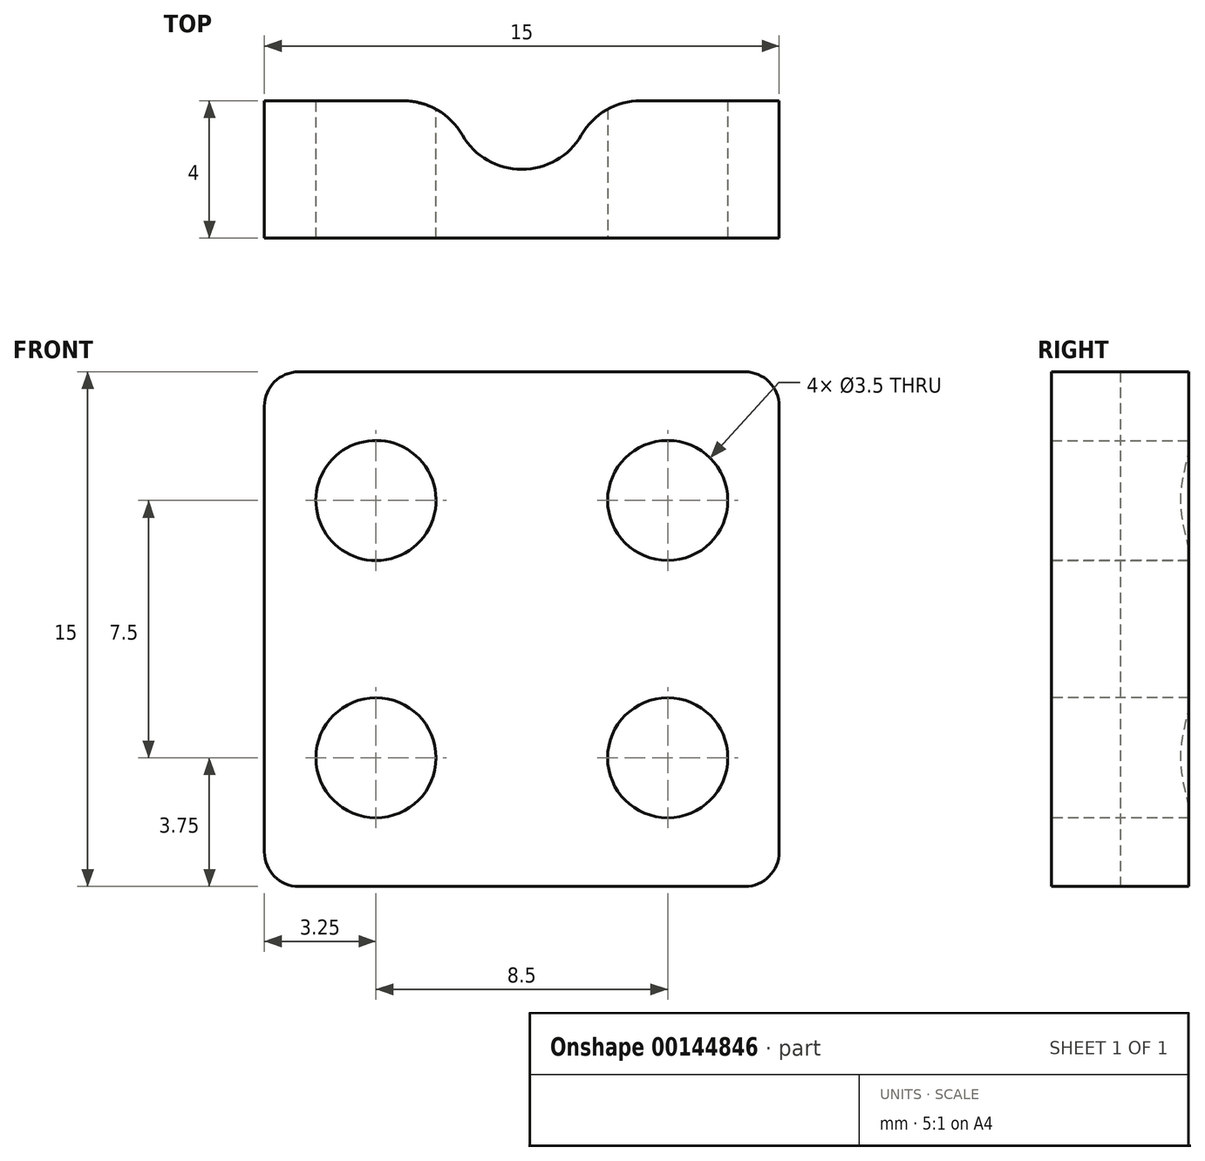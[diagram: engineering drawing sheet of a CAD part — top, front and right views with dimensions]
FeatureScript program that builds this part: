
annotation { "Feature Type Name" : "Feature", "Feature Type Description" : "" }
export const myFeature = defineFeature(function(context is Context, id is Id, definition is map)
    precondition{}
    {
        {
            var Q0;
            Q0=qCreatedBy(makeId("Top.planeOp"),FACE);
            var sketch = newSketch(context, id + "F0", { "sketchPlane" : qUnion([Q0])});
            skLineSegment(sketch, "E0.bottom", {"start": v(7.5, -4) * mm, "end": v(-7.5, -4) * mm});
            skLineSegment(sketch, "E0.top", {"start": v(7.5, 4) * mm, "end": v(-7.5, 4) * mm});
            skLineSegment(sketch, "E0.left", {"start": v(7.5, -4) * mm, "end": v(7.5, 4) * mm});
            skLineSegment(sketch, "E0.right", {"start": v(-7.5, -4) * mm, "end": v(-7.5, 4) * mm});
            skPoint(sketch, "E0.middle", {"position": v(0, 0) * mm});
            skSolve(sketch);
        }
        {
            var Q0;
            Q0=qCreatedBy(makeId("Top.planeOp"),FACE);
            var sketch = newSketch(context, id + "F1", { "sketchPlane" : qUnion([Q0])});
            skCircle(sketch, "E1", {"center": v(0, 0) * mm, "radius": 2 * mm});
            skSolve(sketch);
        }
        {
            var Q0;
            Q0=makeQuery(id+"F0.imprint","IMPRINT",FACE,{"disambiguationData":[TD([[makeQuery(id+"F0.imprint","IMPRINT",EDGE,{"derivedFrom":sQuery(id+"F0.wireOp",EDGE,"E0.bottom")}),-1.0]])]});
            extrude(context, id + "F2", {"entities" : qUnion([Q0]), "depth" : 15 * mm});
        }
        {
            var Q0;
            Q0=makeQuery(id+"F1.imprint","IMPRINT",FACE,{"disambiguationData":[TD([[makeQuery(id+"F1.imprint","IMPRINT",EDGE,{"derivedFrom":sQuery(id+"F1.wireOp",EDGE,"E1")}),1.0]])]});
            extrude(context, id + "F3", {"entities" : qUnion([Q0]), "operationType" : NewBodyOperationType.REMOVE, "depth" : 20 * mm});
        }
        {
            var Q0;
            Q0=qCreatedBy(makeId("Front.planeOp"),FACE);
            var sketch = newSketch(context, id + "F4", { "sketchPlane" : qUnion([Q0])});
            skCircle(sketch, "E2", {"center": v(-4.25, 11.25) * mm, "radius": 1.75 * mm});
            skSolve(sketch);
        }
        {
            var Q0;
            Q0 = qSketchRegion(id + "F4", true);
            extrude(context, id + "F5", {"entities" : qUnion([Q0]), "operationType" : NewBodyOperationType.REMOVE, "depth" : 15 * mm});
        }
        {
            var Q0;
            Q0 = qSketchRegion(id + "F4", true);
            extrude(context, id + "F6", {"entities" : qUnion([Q0]), "operationType" : NewBodyOperationType.REMOVE, "oppositeDirection" : true, "depth" : 25 * mm});
        }
        {
            var Q0;
            Q0=qCreatedBy(makeId("Top.planeOp"),FACE);
            var sketch = newSketch(context, id + "F7", { "sketchPlane" : qUnion([Q0])});
            skLineSegment(sketch, "E3.bottom", {"start": v(9.53, 0) * mm, "end": v(-9.53, 0) * mm});
            skLineSegment(sketch, "E3.top", {"start": v(9.53, 8.77) * mm, "end": v(-9.53, 8.77) * mm});
            skLineSegment(sketch, "E3.left", {"start": v(9.53, 0) * mm, "end": v(9.53, 8.77) * mm});
            skLineSegment(sketch, "E3.right", {"start": v(-9.53, 0) * mm, "end": v(-9.53, 8.77) * mm});
            skPoint(sketch, "E3.middle", {"position": v(0, 4.38) * mm});
            skSolve(sketch);
        }
        {
            var Q0;
            Q0=makeQuery(id+"F2.opExtrude","SWEPT_FACE",FACE,{"disambiguationData":[OSD([sQuery(id+"F0.wireOp",EDGE,"E0.bottom")])]});
            var sketch = newSketch(context, id + "F8", { "sketchPlane" : qUnion([Q0])});
            skCircle(sketch, "E4", {"center": v(-4.25, 3.75) * mm, "radius": 1.75 * mm});
            skSolve(sketch);
        }
        {
            var Q0;
            Q0 = qSketchRegion(id + "F8", true);
            extrude(context, id + "F9", {"entities" : qUnion([Q0]), "operationType" : NewBodyOperationType.REMOVE, "oppositeDirection" : true, "depth" : 25 * mm});
        }
        {
            var Q0;
            Q0=makeQuery(id+"F2.opExtrude","SWEPT_FACE",FACE,{"disambiguationData":[OSD([sQuery(id+"F0.wireOp",EDGE,"E0.bottom")])]});
            var sketch = newSketch(context, id + "F10", { "sketchPlane" : qUnion([Q0])});
            skCircle(sketch, "E5", {"center": v(4.25, 11.25) * mm, "radius": 1.75 * mm});
            skCircle(sketch, "E6", {"center": v(4.25, 3.75) * mm, "radius": 1.75 * mm});
            skSolve(sketch);
        }
        {
            var Q0;
            Q0 = qSketchRegion(id + "F10", true);
            extrude(context, id + "F11", {"entities" : qUnion([Q0]), "operationType" : NewBodyOperationType.REMOVE, "oppositeDirection" : true, "depth" : 25 * mm});
        }
        {
            var Q0;
            Q0 = qSketchRegion(id + "F7", true);
            extrude(context, id + "F12", {"entities" : qUnion([Q0]), "operationType" : NewBodyOperationType.REMOVE, "depth" : 25 * mm});
        }
        {
            var Q0;
            Q0=makeQuery(id+"F12.boolean.opBoolean","INTERSECT",EDGE,{"disambiguationData":[OD(0.0)],"derivedFrom":[makeQuery(id+"F3.boolean.opBoolean","COPY",FACE,{"derivedFrom":makeQuery(id+"F3.opExtrude","SWEPT_FACE",FACE,{"disambiguationData":[OSD([sQuery(id+"F1.wireOp",EDGE,"E1")])]})}),makeQuery(id+"F12.opExtrude","SWEPT_FACE",FACE,{"disambiguationData":[OSD([sQuery(id+"F7.wireOp",EDGE,"E3.bottom")])]})]});
            var Q1;
            Q1=makeQuery(id+"F12.boolean.opBoolean","INTERSECT",EDGE,{"disambiguationData":[OD(1.0)],"derivedFrom":[makeQuery(id+"F3.boolean.opBoolean","COPY",FACE,{"derivedFrom":makeQuery(id+"F3.opExtrude","SWEPT_FACE",FACE,{"disambiguationData":[OSD([sQuery(id+"F1.wireOp",EDGE,"E1")])]})}),makeQuery(id+"F12.opExtrude","SWEPT_FACE",FACE,{"disambiguationData":[OSD([sQuery(id+"F7.wireOp",EDGE,"E3.bottom")])]})]});
            fillet(context, id + "F13", {"entities" : qUnion([Q0, Q1]), "radius" : 2 * mm, "tangentPropagation" : true, "allowEdgeOverflow" : false});
        }
        {
            var Q0;
            Q0=makeQuery(id+"F2.opExtrude","CAP_EDGE",EDGE,{"disambiguationData":[OSD([sQuery(id+"F0.wireOp",EDGE,"E0.right")])],"isStart":false});
            var Q1;
            Q1=makeQuery(id+"F2.opExtrude","CAP_EDGE",EDGE,{"disambiguationData":[OSD([sQuery(id+"F0.wireOp",EDGE,"E0.right")])],"isStart":true});
            var Q2;
            Q2=makeQuery(id+"F2.opExtrude","CAP_EDGE",EDGE,{"disambiguationData":[OSD([sQuery(id+"F0.wireOp",EDGE,"E0.left")])],"isStart":false});
            var Q3;
            Q3=makeQuery(id+"F2.opExtrude","CAP_EDGE",EDGE,{"disambiguationData":[OSD([sQuery(id+"F0.wireOp",EDGE,"E0.left")])],"isStart":true});
            fillet(context, id + "F14", {"entities" : qUnion([Q0, Q1, Q2, Q3]), "radius" : 1 * mm, "tangentPropagation" : true, "allowEdgeOverflow" : false});
        }
    });
